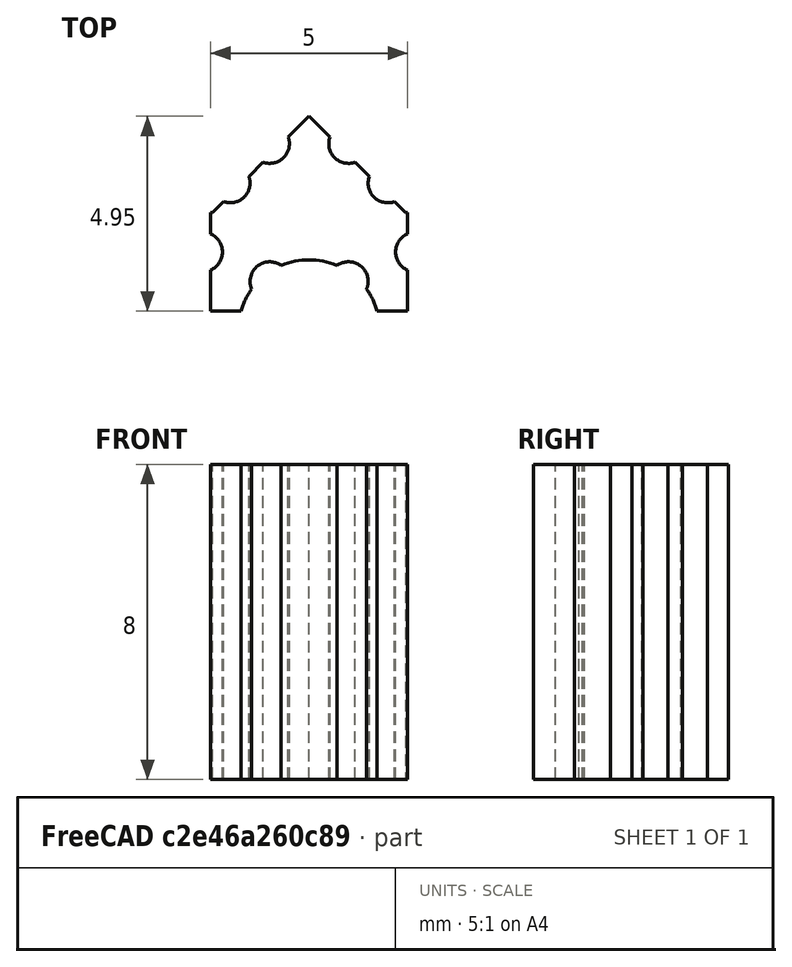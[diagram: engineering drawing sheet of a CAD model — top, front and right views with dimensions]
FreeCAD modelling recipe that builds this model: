
FCSTD DOCUMENT  (FreeCAD 0.15R4671 (Git))
Label: line_fastener_piece
License: All rights reserved
LicenseURL: http://en.wikipedia.org/wiki/All_rights_reserved
objects: Part::Cylinder×9, Part::Box×2, Part::MultiFuse×2, Part::Cut×1
note: 14 computed .brp shape members not serialized (recipe doc carries the construction recipe); baked Part::Feature solids carry a one-line shape summary decoded from their .brp

FEATURE [Part::Box] Box  label="Cube"
  Height = 8
  Length = 3.5
  Placement = pos=(0,-0.5,0) rot=(0,0,1;0.785398rad)
  Width = 3.5
FEATURE [Part::Cylinder] Cylinder001
  Angle = 360
  Height = 8
  Placement = pos=(0,-1,0) rot=(0,0,1;0rad)
  Radius = 1.8
FEATURE [Part::Cylinder] Cylinder002
  Angle = 360
  Height = 10
  Placement = pos=(2,2.75,0) rot=(0,0,1;0rad)
  Radius = 0.5
FEATURE [Part::Cylinder] Cylinder003
  Angle = 360
  Height = 10
  Placement = pos=(1,3.75,0) rot=(0,0,1;0rad)
  Radius = 0.5
FEATURE [Part::Cylinder] Cylinder004
  Angle = 360
  Height = 10
  Placement = pos=(-1,3.75,0) rot=(0,0,1;0rad)
  Radius = 0.5
FEATURE [Part::Cylinder] Cylinder
  Angle = 360
  Height = 10
  Placement = pos=(-2.7,1,0) rot=(0,0,1;0rad)
  Radius = 0.5
FEATURE [Part::Cylinder] Cylinder006
  Angle = 360
  Height = 10
  Placement = pos=(-1,0.25,0) rot=(0,0,1;0rad)
  Radius = 0.5
FEATURE [Part::Cylinder] Cylinder007
  Angle = 360
  Height = 10
  Placement = pos=(2.7,1,0) rot=(0,0,1;0rad)
  Radius = 0.5
FEATURE [Part::Cylinder] Cylinder008
  Angle = 360
  Height = 10
  Placement = pos=(1,0.25,0) rot=(0,0,1;0rad)
  Radius = 0.5
FEATURE [Part::Box] Box001  label="Cube001"
  Height = 8
  Length = 5
  Placement = pos=(-2.5,-0.5,0) rot=(0,0,1;0rad)
  Width = 2.5
FEATURE [Part::Cylinder] Cylinder009
  Angle = 360
  Height = 10
  Placement = pos=(-2,2.75,0) rot=(0,0,1;0rad)
  Radius = 0.5
FEATURE [Part::MultiFuse] Fusion
  Shapes = -> [Box001,Box]
FEATURE [Part::MultiFuse] Fusion001
  Shapes = -> [Cylinder002,Cylinder003,Cylinder,Cylinder004,Cylinder006,Cylinder008,Cylinder001,Cylinder007,Cylinder009]
FEATURE [Part::Cut] Cut
  Base = -> Fusion
  Tool = -> Fusion001
